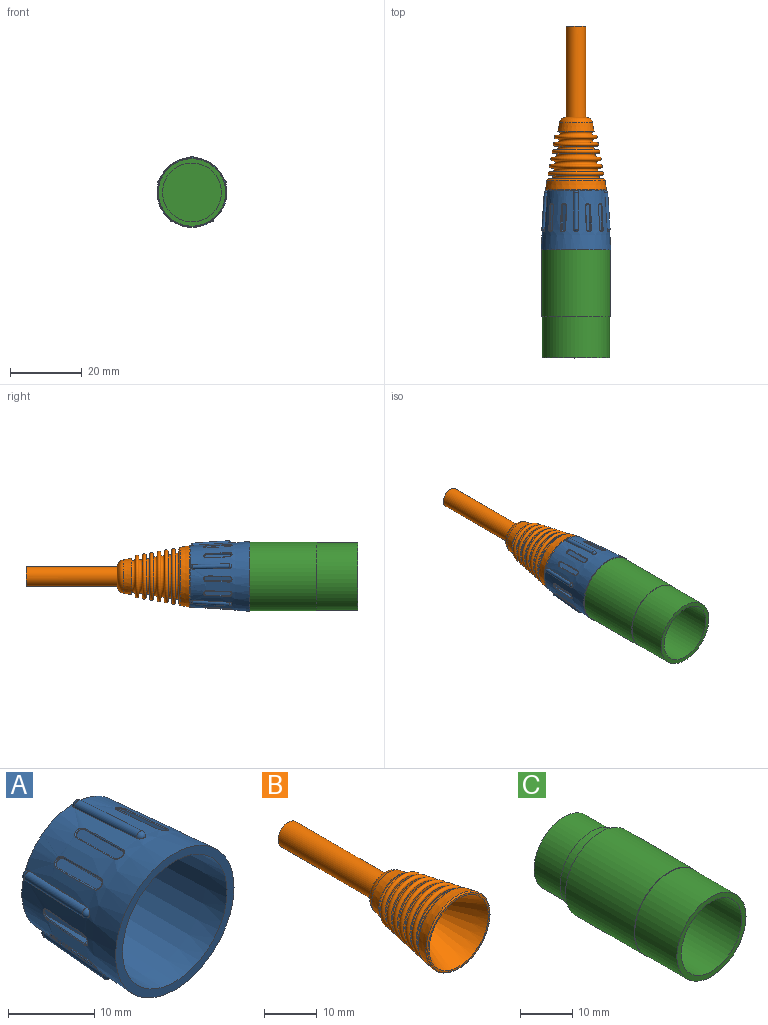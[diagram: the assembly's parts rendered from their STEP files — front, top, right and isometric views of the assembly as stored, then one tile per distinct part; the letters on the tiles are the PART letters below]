
ASSEMBLY  parts=3 mates=2
PART A: 159 faces, bbox 20.2x30x20.1 mm
  f0: cylinder r=0.64mm len=0.64mm, axis (-0.95,-0.07,-0.31), area 0mm2, adj f12,f43,f46
  f1: cylinder r=0.64mm len=0.64mm, axis (-0.95,-0.07,-0.31), area 0mm2, adj f12,f45,f48
  f2: cylinder r=0.64mm len=0.64mm, axis (-0.59,-0.07,0.81), area 0mm2, adj f12,f36,f39
  f3: cylinder r=0.64mm len=0.64mm, axis (-0.59,-0.07,0.81), area 0mm2, adj f12,f38,f41
  f4: cylinder r=0.64mm len=0.64mm, axis (0.59,-0.07,0.81), area 0mm2, adj f12,f29,f32
  f5: cylinder r=0.64mm len=0.64mm, axis (0.59,-0.07,0.81), area 0mm2, adj f12,f31,f34
  f6: cylinder r=0.64mm len=0.64mm, axis (0.95,-0.07,-0.31), area 0mm2, adj f12,f22,f25
  f7: cylinder r=0.64mm len=0.64mm, axis (0.95,-0.07,-0.31), area 0mm2, adj f12,f24,f27
  f8: cylinder r=0.64mm len=0.64mm, axis (0,-0.07,-1), area 0mm2, adj f12,f15,f18
  f9: cylinder r=0.64mm len=0.64mm, axis (0,-0.07,-1), area 0mm2, adj f12,f17,f20
  f10: plane 19.43x19.43mm, normal (0,-1,0), area 65.7mm2, adj f12,f13
  f11: plane 17.15x17.15mm, normal (0,1,0), area 44.3mm2, adj f12,f13
  f12: cone r=9.72mm half-angle=4deg, axis (0,-1,0), area 759.9mm2, adj f0,f1,f2,f3,f4,f5,f6,f7
  f13: cone r=8.57mm half-angle=3deg, axis (0,-1,0), area 845.6mm2, adj f10,f11
  f14: cylinder r=0.64mm len=0.64mm, axis (0,-0.07,-1), area 0mm2, adj f12,f17,f18
  f15: plane 10.14x0.73mm, normal (-1,0,0), area 0.2mm2, adj f8,f12,f16,f19
  f16: cylinder r=0.64mm len=0.64mm, axis (0,-0.07,-1), area 0mm2, adj f12,f15,f20
  f17: plane 10.14x0.73mm, normal (1,0,0), area 0.2mm2, adj f9,f12,f14,f19
  f18: sphere r=0.64mm, area 1.3mm2, adj f8,f14,f19
  f19: cylinder r=0.64mm len=10.18mm, axis (0,-1,0.07), area 20.3mm2, adj f15,f17,f18,f20
  f20: sphere r=0.64mm, area 1.3mm2, adj f9,f16,f19
  f21: cylinder r=0.64mm len=0.64mm, axis (0.95,-0.07,-0.31), area 0mm2, adj f12,f24,f25
  f22: plane 10.14x0.69mm, normal (-0.31,0,-0.95), area 0.2mm2, adj f6,f12,f23,f26
  f23: cylinder r=0.64mm len=0.64mm, axis (0.95,-0.07,-0.31), area 0mm2, adj f12,f22,f27
  f24: plane 10.14x0.69mm, normal (0.31,0,0.95), area 0.2mm2, adj f7,f12,f21,f26
  f25: sphere r=0.64mm, area 1.3mm2, adj f6,f21,f26
  f26: cylinder r=0.64mm len=10.18mm, axis (-0.07,-1,0.02), area 20.3mm2, adj f22,f24,f25,f27
  f27: sphere r=0.64mm, area 1.3mm2, adj f7,f23,f26
  f28: cylinder r=0.64mm len=0.64mm, axis (0.59,-0.07,0.81), area 0mm2, adj f12,f31,f32
  f29: plane 10.14x0.59mm, normal (0.81,0,-0.59), area 0.2mm2, adj f4,f12,f30,f33
  f30: cylinder r=0.64mm len=0.64mm, axis (0.59,-0.07,0.81), area 0mm2, adj f12,f29,f34
  f31: plane 10.14x0.59mm, normal (-0.81,0,0.59), area 0.2mm2, adj f5,f12,f28,f33
  f32: sphere r=0.64mm, area 1.3mm2, adj f4,f28,f33
  f33: cylinder r=0.64mm len=10.18mm, axis (-0.04,-1,-0.06), area 20.3mm2, adj f29,f31,f32,f34
  f34: sphere r=0.64mm, area 1.3mm2, adj f5,f30,f33
  f35: cylinder r=0.64mm len=0.64mm, axis (-0.59,-0.07,0.81), area 0mm2, adj f12,f38,f39
  f36: plane 10.14x0.59mm, normal (0.81,0,0.59), area 0.2mm2, adj f2,f12,f37,f40
  f37: cylinder r=0.64mm len=0.64mm, axis (-0.59,-0.07,0.81), area 0mm2, adj f12,f36,f41
  f38: plane 10.14x0.59mm, normal (-0.81,0,-0.59), area 0.2mm2, adj f3,f12,f35,f40
  f39: sphere r=0.64mm, area 1.3mm2, adj f2,f35,f40
  f40: cylinder r=0.64mm len=10.18mm, axis (0.04,-1,-0.06), area 20.3mm2, adj f36,f38,f39,f41
  f41: sphere r=0.64mm, area 1.3mm2, adj f3,f37,f40
  f42: cylinder r=0.64mm len=0.64mm, axis (-0.95,-0.07,-0.31), area 0mm2, adj f12,f45,f46
  f43: plane 10.14x0.69mm, normal (-0.31,0,0.95), area 0.2mm2, adj f0,f12,f44,f47
  f44: cylinder r=0.64mm len=0.64mm, axis (-0.95,-0.07,-0.31), area 0mm2, adj f12,f43,f48
  f45: plane 10.14x0.69mm, normal (0.31,0,-0.95), area 0.2mm2, adj f1,f12,f42,f47
  f46: sphere r=0.64mm, area 1.3mm2, adj f0,f42,f47
  f47: cylinder r=0.64mm len=10.18mm, axis (0.07,-1,0.02), area 20.3mm2, adj f43,f45,f46,f48
  f48: sphere r=0.64mm, area 1.3mm2, adj f1,f44,f47
  f49: cylinder r=0.64mm len=0.85mm, axis (0,0,-1), area 0.2mm2, adj f52,f53,f65
  f50: plane 4.89x0.36mm, normal (1,0,0), area 0.9mm2, adj f51,f53,f70
  f51: cylinder r=0.64mm len=1.27mm, axis (0,0,-1), area 1.2mm2, adj f50,f52,f53,f68
  f52: plane 6.35x0.72mm, normal (-1,0,0), area 3.1mm2, adj f49,f51,f53,f66
  f53: plane 7.64x1.29mm, normal (0,0,-1), area 9.3mm2, adj f49,f50,f51,f52,f67,f69
  f54: cylinder r=0.64mm len=0.85mm, axis (0,0,-1), area 0.2mm2, adj f55,f58,f59
  f55: plane 6.35x0.72mm, normal (1,0,0), area 3.1mm2, adj f54,f56,f58,f60
  f56: cylinder r=0.64mm len=1.27mm, axis (0,0,-1), area 1.2mm2, adj f55,f57,f58,f62
  f57: plane 4.89x0.36mm, normal (-1,0,0), area 0.9mm2, adj f56,f58,f64
  f58: plane 7.64x1.29mm, normal (0,0,-1), area 9.3mm2, adj f54,f55,f56,f57,f61,f63
  f59: bspline ~1.16x0.87mm, area 0.3mm2, adj f12,f54,f60,f61
  f60: bspline ~20.47x1.56mm, area 1.1mm2, adj f12,f55,f59,f62
  f61: bspline ~0.8x0.63mm, area 0.1mm2, adj f12,f58,f59,f63
  f62: bspline ~1.55x0.93mm, area 0.4mm2, adj f12,f56,f60,f64
  f63: bspline ~1.94x0.2mm, area 0.3mm2, adj f12,f58,f61,f64
  f64: bspline ~22.89x1.84mm, area 1.2mm2, adj f12,f57,f62,f63
  f65: bspline ~1.16x0.87mm, area 0.3mm2, adj f12,f49,f66,f67
  f66: bspline ~29.95x2.22mm, area 1.1mm2, adj f12,f52,f65,f68
  f67: bspline ~0.8x0.63mm, area 0.1mm2, adj f12,f53,f65,f69
  f68: bspline ~1.55x0.93mm, area 0.4mm2, adj f12,f51,f66,f70
  f69: bspline ~1.94x0.2mm, area 0.3mm2, adj f12,f53,f67,f70
  f70: bspline ~22.89x1.84mm, area 1.2mm2, adj f12,f50,f68,f69
  f71: cylinder r=0.64mm len=0.89mm, axis (0.95,0,-0.31), area 0.2mm2, adj f74,f75,f87
  f72: plane 4.89x0.34mm, normal (0.31,0,0.95), area 0.9mm2, adj f73,f75,f92
  f73: cylinder r=0.64mm len=1.43mm, axis (0.95,0,-0.31), area 1.2mm2, adj f72,f74,f75,f90
  f74: plane 6.35x0.68mm, normal (-0.31,0,-0.95), area 3.1mm2, adj f71,f73,f75,f88
  f75: plane 7.64x1.23mm, normal (0.95,0,-0.31), area 9.3mm2, adj f71,f72,f73,f74,f89,f91
  f76: cylinder r=0.64mm len=0.89mm, axis (0.95,0,-0.31), area 0.2mm2, adj f77,f80,f81
  f77: plane 6.35x0.68mm, normal (0.31,0,0.95), area 3.1mm2, adj f76,f78,f80,f82
  f78: cylinder r=0.64mm len=1.43mm, axis (0.95,0,-0.31), area 1.2mm2, adj f77,f79,f80,f84
  f79: plane 4.89x0.34mm, normal (-0.31,0,-0.95), area 0.9mm2, adj f78,f80,f86
  f80: plane 7.64x1.23mm, normal (0.95,0,-0.31), area 9.3mm2, adj f76,f77,f78,f79,f83,f85
  f81: bspline ~1.2x0.87mm, area 0.3mm2, adj f12,f76,f82,f83
  f82: bspline ~20.47x1.47mm, area 1.1mm2, adj f12,f77,f81,f84
  f83: bspline ~0.8x0.6mm, area 0.1mm2, adj f12,f80,f81,f85
  f84: bspline ~1.58x0.93mm, area 0.4mm2, adj f12,f78,f82,f86
  f85: bspline ~1.94x0.22mm, area 0.3mm2, adj f12,f80,f83,f86
  f86: bspline ~22.89x1.75mm, area 1.2mm2, adj f12,f79,f84,f85
  f87: bspline ~1.01x0.87mm, area 0.3mm2, adj f12,f71,f88,f89
  f88: bspline ~29.95x2.15mm, area 1.1mm2, adj f12,f74,f87,f90
  f89: bspline ~0.8x0.6mm, area 0.1mm2, adj f12,f75,f87,f91
  f90: bspline ~1.36x0.93mm, area 0.4mm2, adj f12,f73,f88,f92
  f91: bspline ~1.94x0.22mm, area 0.3mm2, adj f12,f75,f89,f92
  f92: bspline ~22.89x1.75mm, area 1.2mm2, adj f12,f72,f90,f91
  f93: cylinder r=0.64mm len=0.84mm, axis (0.59,0,0.81), area 0.2mm2, adj f96,f97,f109
  f94: plane 4.89x0.29mm, normal (-0.81,0,0.59), area 0.9mm2, adj f95,f97,f114
  f95: cylinder r=0.64mm len=1.45mm, axis (0.59,0,0.81), area 1.2mm2, adj f94,f96,f97,f112
  f96: plane 6.35x0.58mm, normal (0.81,0,-0.59), area 3.1mm2, adj f93,f95,f97,f110
  f97: plane 7.64x1.05mm, normal (0.59,0,0.81), area 9.3mm2, adj f93,f94,f95,f96,f111,f113
  f98: cylinder r=0.64mm len=0.84mm, axis (0.59,0,0.81), area 0.2mm2, adj f99,f102,f103
  f99: plane 6.35x0.58mm, normal (-0.81,0,0.59), area 3.1mm2, adj f98,f100,f102,f104
  f100: cylinder r=0.64mm len=1.45mm, axis (0.59,0,0.81), area 1.2mm2, adj f99,f101,f102,f106
  f101: plane 4.89x0.29mm, normal (0.81,0,-0.59), area 0.9mm2, adj f100,f102,f108
  f102: plane 7.64x1.05mm, normal (0.59,0,0.81), area 9.3mm2, adj f98,f99,f100,f101,f105,f107
  f103: bspline ~1.12x0.87mm, area 0.3mm2, adj f12,f98,f104,f105
  f104: bspline ~20.47x1.25mm, area 1.1mm2, adj f12,f99,f103,f106
  f105: bspline ~0.8x0.56mm, area 0.1mm2, adj f12,f102,f103,f107
  f106: bspline ~1.47x0.93mm, area 0.4mm2, adj f12,f100,f104,f108
  f107: bspline ~1.94x0.23mm, area 0.3mm2, adj f12,f102,f105,f108
  f108: bspline ~22.89x1.54mm, area 1.2mm2, adj f12,f101,f106,f107
  f109: bspline ~0.97x0.87mm, area 0.3mm2, adj f12,f93,f110,f111
  f110: bspline ~29.95x1.86mm, area 1.1mm2, adj f12,f96,f109,f112
  f111: bspline ~0.8x0.52mm, area 0.1mm2, adj f12,f97,f109,f113
  f112: bspline ~1.21x1.04mm, area 0.4mm2, adj f12,f95,f110,f114
  f113: bspline ~1.94x0.24mm, area 0.3mm2, adj f12,f97,f111,f114
  f114: bspline ~22.89x1.49mm, area 1.2mm2, adj f12,f94,f112,f113
  f115: cylinder r=0.64mm len=0.84mm, axis (-0.59,0,0.81), area 0.2mm2, adj f118,f119,f131
  f116: plane 4.89x0.29mm, normal (-0.81,0,-0.59), area 0.9mm2, adj f117,f119,f136
  f117: cylinder r=0.64mm len=1.45mm, axis (-0.59,0,0.81), area 1.2mm2, adj f116,f118,f119,f134
  f118: plane 6.35x0.58mm, normal (0.81,0,0.59), area 3.1mm2, adj f115,f117,f119,f132
  f119: plane 7.64x1.05mm, normal (-0.59,0,0.81), area 9.3mm2, adj f115,f116,f117,f118,f133,f135
  f120: cylinder r=0.64mm len=0.84mm, axis (-0.59,0,0.81), area 0.2mm2, adj f121,f124,f125
  f121: plane 6.35x0.58mm, normal (-0.81,0,-0.59), area 3.1mm2, adj f120,f122,f124,f126
  f122: cylinder r=0.64mm len=1.45mm, axis (-0.59,0,0.81), area 1.2mm2, adj f121,f123,f124,f128
  f123: plane 4.89x0.29mm, normal (0.81,0,0.59), area 0.9mm2, adj f122,f124,f130
  f124: plane 7.64x1.05mm, normal (-0.59,0,0.81), area 9.3mm2, adj f120,f121,f122,f123,f127,f129
  f125: bspline ~0.97x0.87mm, area 0.3mm2, adj f12,f120,f126,f127
  f126: bspline ~20.47x1.32mm, area 1.1mm2, adj f12,f121,f125,f128
  f127: bspline ~0.8x0.52mm, area 0.1mm2, adj f12,f124,f125,f129
  f128: bspline ~1.21x1.04mm, area 0.4mm2, adj f12,f122,f126,f130
  f129: bspline ~1.94x0.24mm, area 0.3mm2, adj f12,f124,f127,f130
  f130: bspline ~22.89x1.49mm, area 1.2mm2, adj f12,f123,f128,f129
  f131: bspline ~1.12x0.87mm, area 0.3mm2, adj f12,f115,f132,f133
  f132: bspline ~29.95x1.79mm, area 1.1mm2, adj f12,f118,f131,f134
  f133: bspline ~0.8x0.56mm, area 0.1mm2, adj f12,f119,f131,f135
  f134: bspline ~1.47x0.93mm, area 0.4mm2, adj f12,f117,f132,f136
  f135: bspline ~1.94x0.23mm, area 0.3mm2, adj f12,f119,f133,f136
  f136: bspline ~22.89x1.54mm, area 1.2mm2, adj f12,f116,f134,f135
  f137: cylinder r=0.64mm len=0.89mm, axis (-0.95,0,-0.31), area 0.2mm2, adj f140,f141,f153
  f138: plane 4.89x0.34mm, normal (0.31,0,-0.95), area 0.9mm2, adj f139,f141,f158
  f139: cylinder r=0.64mm len=1.43mm, axis (-0.95,0,-0.31), area 1.2mm2, adj f138,f140,f141,f156
  f140: plane 6.35x0.68mm, normal (-0.31,0,0.95), area 3.1mm2, adj f137,f139,f141,f154
  f141: plane 7.64x1.23mm, normal (-0.95,0,-0.31), area 9.3mm2, adj f137,f138,f139,f140,f155,f157
  f142: cylinder r=0.64mm len=0.89mm, axis (-0.95,0,-0.31), area 0.2mm2, adj f143,f146,f147
  f143: plane 6.35x0.68mm, normal (0.31,0,-0.95), area 3.1mm2, adj f142,f144,f146,f148
  f144: cylinder r=0.64mm len=1.43mm, axis (-0.95,0,-0.31), area 1.2mm2, adj f143,f145,f146,f150
  f145: plane 4.89x0.34mm, normal (-0.31,0,0.95), area 0.9mm2, adj f144,f146,f152
  f146: plane 7.64x1.23mm, normal (-0.95,0,-0.31), area 9.3mm2, adj f142,f143,f144,f145,f149,f151
  f147: bspline ~1.01x0.87mm, area 0.3mm2, adj f12,f142,f148,f149
  f148: bspline ~20.47x1.51mm, area 1.1mm2, adj f12,f143,f147,f150
  f149: bspline ~0.8x0.6mm, area 0.1mm2, adj f12,f146,f147,f151
  f150: bspline ~1.36x0.93mm, area 0.4mm2, adj f12,f144,f148,f152
  f151: bspline ~1.94x0.22mm, area 0.3mm2, adj f12,f146,f149,f152
  f152: bspline ~22.89x1.75mm, area 1.2mm2, adj f12,f145,f150,f151
  f153: bspline ~1.2x0.87mm, area 0.3mm2, adj f12,f137,f154,f155
  f154: bspline ~29.95x2.1mm, area 1.1mm2, adj f12,f140,f153,f156
  f155: bspline ~0.8x0.6mm, area 0.1mm2, adj f12,f141,f153,f157
  f156: bspline ~1.58x0.93mm, area 0.4mm2, adj f12,f139,f154,f158
  f157: bspline ~1.94x0.22mm, area 0.3mm2, adj f12,f141,f155,f158
  f158: bspline ~22.89x1.75mm, area 1.2mm2, adj f12,f138,f156,f157
PART B: 36 faces, bbox 18.5x45.7x18.5 mm
  f0: cone r=8.57mm half-angle=10deg, axis (0,-1,0), area 130.2mm2, adj f31,f35
  f1: plane 16.54x16.54mm, normal (0,-1,0), area 16.9mm2, adj f32,f35
  f2: plane 14.46x14.46mm, normal (0,-1,0), area 14.9mm2, adj f4,f30
  f3: plane 15.17x15.17mm, normal (0,1,0), area 31.6mm2, adj f4,f31
  f4: torus R=6.89mm, axis (0,-1,0), area 65.9mm2, adj f2,f3
  f5: plane 13.74x13.74mm, normal (0,-1,0), area 14.2mm2, adj f7,f29
  f6: plane 14.46x14.46mm, normal (0,1,0), area 30mm2, adj f7,f30
  f7: torus R=6.53mm, axis (0,-1,0), area 62.3mm2, adj f5,f6
  f8: plane 13.02x13.02mm, normal (0,-1,0), area 13.4mm2, adj f10,f28
  f9: plane 13.74x13.74mm, normal (0,1,0), area 28.5mm2, adj f10,f29
  f10: torus R=6.17mm, axis (0,-1,0), area 58.7mm2, adj f8,f9
  f11: plane 12.31x12.31mm, normal (0,-1,0), area 12.7mm2, adj f13,f27
  f12: plane 13.02x13.02mm, normal (0,1,0), area 26.9mm2, adj f13,f28
  f13: torus R=5.82mm, axis (0,-1,0), area 55.1mm2, adj f11,f12
  f14: plane 11.59x11.59mm, normal (0,-1,0), area 11.9mm2, adj f16,f26
  f15: plane 12.31x12.31mm, normal (0,1,0), area 25.4mm2, adj f16,f27
  f16: torus R=5.46mm, axis (0,-1,0), area 51.5mm2, adj f14,f15
  f17: plane 10.87x10.87mm, normal (0,-1,0), area 11.1mm2, adj f19,f25
  f18: plane 11.59x11.59mm, normal (0,1,0), area 23.8mm2, adj f19,f26
  f19: torus R=5.1mm, axis (0,-1,0), area 47.9mm2, adj f17,f18
  f20: plane 10.87x10.87mm, normal (0,1,0), area 18mm2, adj f22,f25
  f21: plane 10.1x10.1mm, normal (0,-1,0), area 5.3mm2, adj f22,f23
  f22: torus R=4.88mm, axis (0,-1,0), area 45.7mm2, adj f20,f21
  f23: cone r=5.23mm half-angle=10deg, axis (0,-1,0), area 73mm2, adj f21,f24
  f24: torus R=2.76mm, axis (0,-1,0), area 64.9mm2, adj f23,f33
  f25: torus R=5.44mm, axis (0,1,0), area 57.8mm2, adj f17,f20
  f26: torus R=5.79mm, axis (0,1,0), area 61.4mm2, adj f14,f18
  f27: torus R=6.15mm, axis (0,1,0), area 64.9mm2, adj f11,f15
  f28: torus R=6.51mm, axis (0,1,0), area 68.5mm2, adj f8,f12
  f29: torus R=6.87mm, axis (0,1,0), area 72.1mm2, adj f5,f9
  f30: torus R=7.23mm, axis (0,1,0), area 75.7mm2, adj f2,f6
  f31: torus R=7.59mm, axis (0,1,0), area 35.2mm2, adj f0,f3
  f32: cone r=7.94mm half-angle=25deg, axis (0,-1,0), area 468.3mm2, adj f1
  f33: cylinder r=2.75mm len=25.4mm, axis (0,-1,0), area 438.9mm2, adj f24,f34
  f34: plane 5.5x5.5mm, normal (0,1,0), area 23.8mm2, adj f33
  f35: torus R=8.27mm, axis (0,-1,0), area 23.5mm2, adj f0,f1
PART C: 13 faces, bbox 19x40x19 mm
  f0: cylinder r=9.37mm len=18.75mm, axis (0,-1,0), area 673.1mm2, adj f1,f4
  f1: plane 18.75x18.75mm, normal (0,-1,0), area 65.2mm2, adj f0,f9
  f2: cylinder r=9.5mm len=19mm, axis (0,-1,0), area 1114.3mm2, adj f3,f4
  f3: plane 19x19mm, normal (0,1,0), area 62.8mm2, adj f2,f5
  f4: plane 19x19mm, normal (0,-1,0), area 7.5mm2, adj f0,f2
  f5: cylinder r=8.38mm len=16.76mm, axis (0,-1,0), area 133.8mm2, adj f3,f6
  f6: plane 16.76x16.76mm, normal (0,1,0), area 13.2mm2, adj f5,f7
  f7: cylinder r=8.13mm len=16.26mm, axis (0,-1,0), area 376.2mm2, adj f6,f8
  f8: plane 16.26x16.26mm, normal (0,1,0), area 54.3mm2, adj f7,f11
  f9: cylinder r=8.19mm len=16.38mm, axis (0,-1,0), area 686.3mm2, adj f1,f10
  f10: plane 16.38x16.38mm, normal (0,-1,0), area 210.8mm2, adj f9
  f11: cylinder r=6.99mm len=25.15mm, axis (0,1,0), area 1103.6mm2, adj f8,f12
  f12: plane 13.97x13.97mm, normal (0,1,0), area 153.3mm2, adj f11
PLACE A t=(0,30.1,0)mm
PLACE B t=(0,46.61,0)mm
PLACE C at identity
MATE revolute A.f12 <-> C.f0  axis (0,-1,0) through (0,30.1,0)mm
MATE revolute B.f0 <-> A.f12  axis (0,-1,0) through (0,46.61,0)mm
